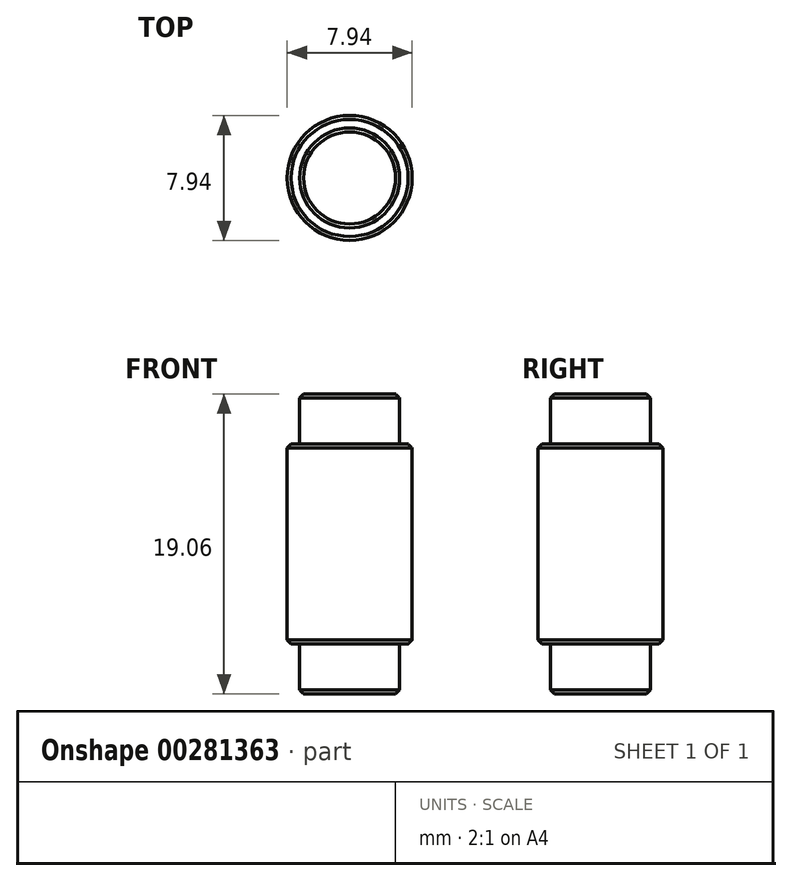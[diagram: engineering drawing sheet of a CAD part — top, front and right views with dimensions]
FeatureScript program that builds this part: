
annotation { "Feature Type Name" : "Feature", "Feature Type Description" : "" }
export const myFeature = defineFeature(function(context is Context, id is Id, definition is map)
    precondition{}
    {
        {
            var Q0;
            Q0=qCreatedBy(makeId("Top.planeOp"),FACE);
            var sketch = newSketch(context, id + "F0", { "sketchPlane" : qUnion([Q0])});
            skCircle(sketch, "E0", {"center": v(0, 0) * mm, "radius": 3.18 * mm});
            skCircle(sketch, "E1", {"center": v(0, 0) * mm, "radius": 3.97 * mm});
            skSolve(sketch);
        }
        {
            var Q0;
            Q0=makeQuery(id+"F0.imprint","IMPRINT",FACE,{"disambiguationData":[TD([[makeQuery(id+"F0.imprint","IMPRINT",EDGE,{"derivedFrom":sQuery(id+"F0.wireOp",EDGE,"E0")}),-1.0]])]});
            var Q1;
            Q1=makeQuery(id+"F0.imprint","IMPRINT",FACE,{"disambiguationData":[TD([[makeQuery(id+"F0.imprint","IMPRINT",EDGE,{"derivedFrom":sQuery(id+"F0.wireOp",EDGE,"E0")}),1.0]])]});
            extrude(context, id + "F1", {"entities" : qUnion([Q0, Q1]), "depth" : 12.7 * mm});
        }
        {
            var Q0;
            Q0=makeQuery(id+"F1.opExtrude","CAP_FACE",FACE,{"disambiguationData":[OSD([sQuery(id+"F0.wireOp",EDGE,"E1")])],"isStart":true});
            var sketch = newSketch(context, id + "F2", { "sketchPlane" : qUnion([Q0])});
            skCircle(sketch, "E2", {"center": v(0, 0) * mm, "radius": 3.18 * mm});
            skSolve(sketch);
        }
        {
            var Q0;
            Q0 = qSketchRegion(id + "F2", true);
            extrude(context, id + "F3", {"entities" : qUnion([Q0]), "operationType" : NewBodyOperationType.ADD, "depth" : 3.17 * mm});
        }
        {
            var Q0;
            Q0=makeQuery(id+"F1.opExtrude","CAP_FACE",FACE,{"disambiguationData":[OSD([sQuery(id+"F0.wireOp",EDGE,"E1")])],"isStart":false});
            var sketch = newSketch(context, id + "F4", { "sketchPlane" : qUnion([Q0])});
            skCircle(sketch, "E3", {"center": v(0, 0) * mm, "radius": 3.18 * mm});
            skSolve(sketch);
        }
        {
            var Q0;
            Q0 = qSketchRegion(id + "F4", true);
            extrude(context, id + "F5", {"entities" : qUnion([Q0]), "operationType" : NewBodyOperationType.ADD, "depth" : 3.17 * mm});
        }
        {
            var Q0;
            Q0=makeQuery(id+"F5.opExtrude","CAP_EDGE",EDGE,{"disambiguationData":[OSD([sQuery(id+"F4.wireOp",EDGE,"E3")])],"isStart":false});
            var Q1;
            Q1=makeQuery(id+"F1.opExtrude","CAP_EDGE",EDGE,{"disambiguationData":[OSD([sQuery(id+"F0.wireOp",EDGE,"E1")])],"isStart":false});
            var Q2;
            Q2=makeQuery(id+"F1.opExtrude","CAP_EDGE",EDGE,{"disambiguationData":[OSD([sQuery(id+"F0.wireOp",EDGE,"E1")])],"isStart":true});
            var Q3;
            Q3=makeQuery(id+"F3.opExtrude","CAP_EDGE",EDGE,{"disambiguationData":[OSD([sQuery(id+"F2.wireOp",EDGE,"E2")])],"isStart":false});
            chamfer(context, id + "F6", {"entities" : qUnion([Q0, Q1, Q2, Q3]), "width" : 0.25 * mm, "tangentPropagation" : true});
        }
    });
